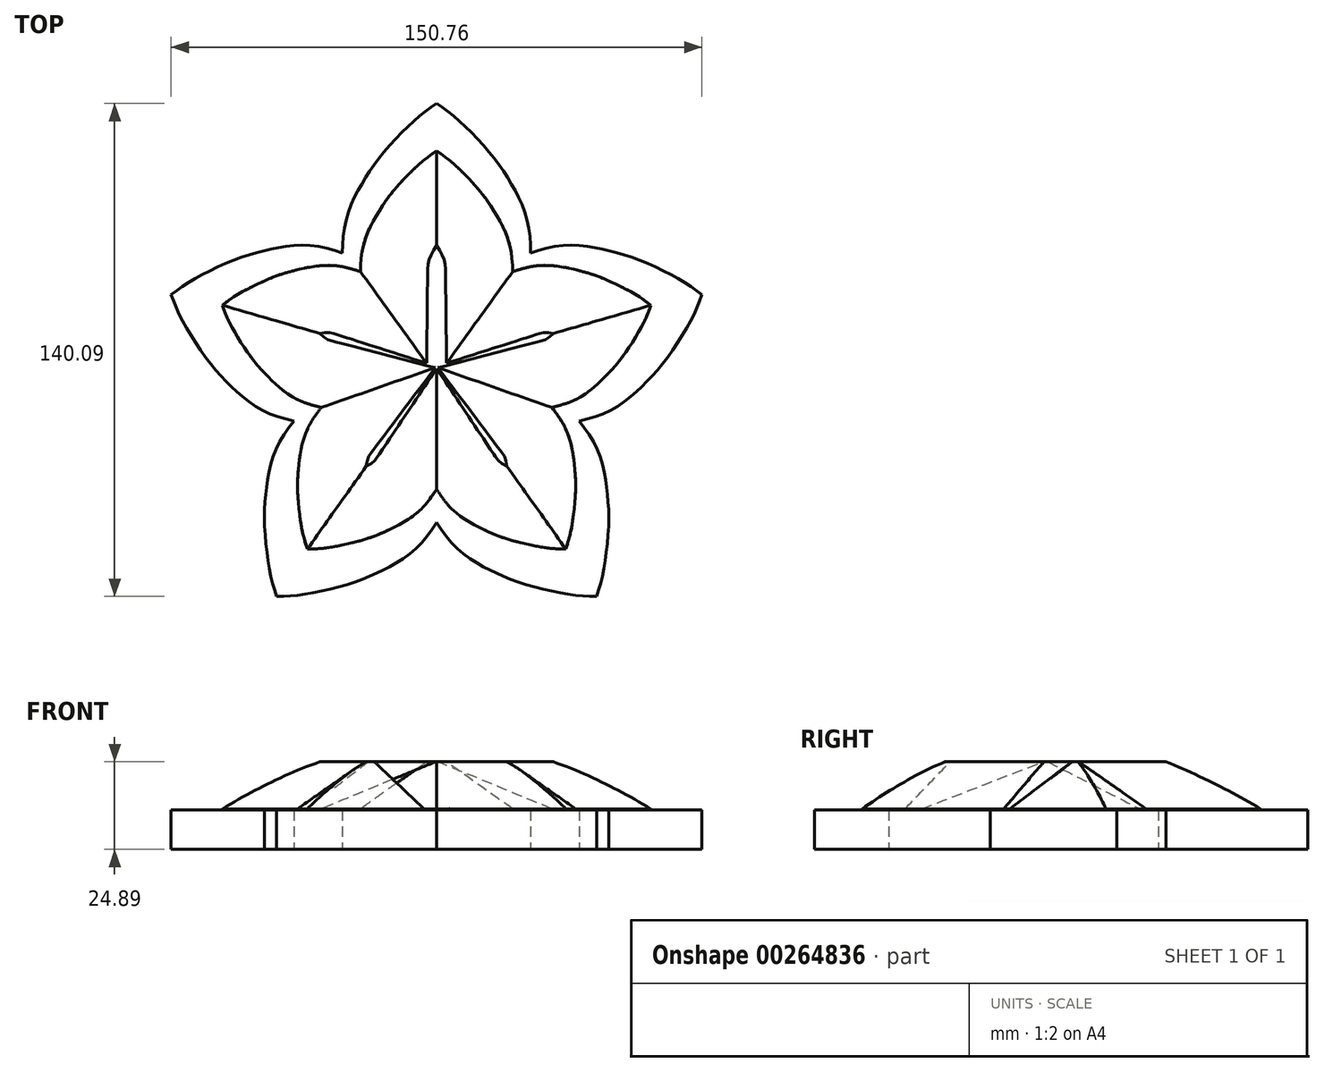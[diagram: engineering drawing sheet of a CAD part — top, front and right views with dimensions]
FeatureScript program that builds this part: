
annotation { "Feature Type Name" : "Feature", "Feature Type Description" : "" }
export const myFeature = defineFeature(function(context is Context, id is Id, definition is map)
    precondition{}
    {
        {
            var Q0;
            Q0=qCreatedBy(makeId("Top.planeOp"),FACE);
            var sketch = newSketch(context, id + "F0", { "sketchPlane" : qUnion([Q0])});
            skFitSpline(sketch, "E0.MirrorCS", {"points": [v(19.73, 114.61) * mm, v(16.52, 127.07) * mm, v(9.03, 139.64) * mm, v(3.16, 145.12) * mm, v(0, 146.87) * mm], "startDerivative": vector(-4.34, 40.29) * mm, "endDerivative": vector(-28.01, 11.55) * mm, "construction": true});
            skLineSegment(sketch, "E1", {"start": v(0, 0) * mm, "end": v(0, 146.87) * mm, "construction": true});
            skFitSpline(sketch, "E2.MirrorCS", {"points": [v(-19.73, 114.61) * mm, v(-16.52, 127.07) * mm, v(-9.03, 139.64) * mm, v(-3.16, 145.12) * mm, v(0, 146.87) * mm], "startDerivative": vector(4.34, 40.29) * mm, "endDerivative": vector(28.01, 11.55) * mm, "construction": true});
            skLineSegment(sketch, "E3", {"start": v(0, 0) * mm, "end": v(0, 0) * mm});
            skFitSpline(sketch, "E4.MirrorCS", {"points": [v(-19.73, 114.61) * mm, v(-32.36, 116) * mm, v(-46.75, 113.44) * mm, v(-53.96, 109.89) * mm, v(-56.85, 107.42) * mm], "startDerivative": vector(-39.26, 10.04) * mm, "endDerivative": vector(-20.62, -22.2) * mm, "construction": true});
            skFitSpline(sketch, "E5.MirrorCS", {"points": [v(-33.54, 77.65) * mm, v(-43.99, 84.88) * mm, v(-53.18, 96.25) * mm, v(-56.28, 103.66) * mm, v(-56.85, 107.42) * mm], "startDerivative": vector(-36.22, 18.17) * mm, "endDerivative": vector(-1, 30.28) * mm, "construction": true});
            skFitSpline(sketch, "E6.MirrorCS", {"points": [v(19.73, 114.61) * mm, v(32.36, 116) * mm, v(46.75, 113.44) * mm, v(53.96, 109.89) * mm, v(56.85, 107.42) * mm], "startDerivative": vector(39.26, 10.04) * mm, "endDerivative": vector(20.62, -22.2) * mm, "construction": true});
            skFitSpline(sketch, "E7.MirrorCS", {"points": [v(33.54, 77.65) * mm, v(43.99, 84.88) * mm, v(53.18, 96.25) * mm, v(56.28, 103.66) * mm, v(56.85, 107.42) * mm], "startDerivative": vector(36.22, 18.17) * mm, "endDerivative": vector(1, 30.28) * mm, "construction": true});
            skFitSpline(sketch, "E8.MirrorCS", {"points": [v(-33.54, 77.65) * mm, v(-39.27, 66.3) * mm, v(-41.91, 51.92) * mm, v(-41.1, 43.93) * mm, v(-39.8, 40.36) * mm], "startDerivative": vector(-23.15, -33.26) * mm, "endDerivative": vector(13.58, -27.09) * mm, "construction": true});
            skFitSpline(sketch, "E9.MirrorCS", {"points": [v(-3.76, 51.77) * mm, v(-14.18, 44.51) * mm, v(-28.06, 39.89) * mm, v(-36.09, 39.57) * mm, v(-39.8, 40.36) * mm], "startDerivative": vector(-29.7, -27.57) * mm, "endDerivative": vector(-28.72, 9.66) * mm, "construction": true});
            skFitSpline(sketch, "E10.MirrorCS", {"points": [v(33.54, 77.65) * mm, v(39.27, 66.3) * mm, v(41.91, 51.92) * mm, v(41.1, 43.93) * mm, v(39.8, 40.36) * mm], "startDerivative": vector(23.15, -33.26) * mm, "endDerivative": vector(-13.58, -27.09) * mm, "construction": true});
            skFitSpline(sketch, "E11.MirrorCS", {"points": [v(3.76, 51.77) * mm, v(14.18, 44.51) * mm, v(28.06, 39.89) * mm, v(36.09, 39.57) * mm, v(39.8, 40.36) * mm], "startDerivative": vector(29.7, -27.57) * mm, "endDerivative": vector(28.72, 9.66) * mm, "construction": true});
            skFitSpline(sketch, "E12", {"points": [v(-19.88, 115.85) * mm, v(-16.52, 127.07) * mm, v(-9.03, 139.64) * mm, v(-3.16, 145.12) * mm, v(0, 146.87) * mm], "startDerivative": vector(8.84, 38.02) * mm, "endDerivative": vector(19.62, 9.54) * mm, "construction": true});
            skFitSpline(sketch, "E13.MirrorCS", {"points": [v(19.88, 115.85) * mm, v(16.52, 127.07) * mm, v(9.03, 139.64) * mm, v(3.16, 145.12) * mm, v(0, 146.87) * mm], "startDerivative": vector(-8.84, 38.02) * mm, "endDerivative": vector(-19.62, 9.54) * mm, "construction": true});
            skLineSegment(sketch, "E14", {"start": v(-19.88, 115.85) * mm, "end": v(0, 87.57) * mm, "construction": true});
            skLineSegment(sketch, "E15", {"start": v(0, 87.57) * mm, "end": v(19.88, 115.85) * mm, "construction": true});
            skFitSpline(sketch, "E16.MirrorCS", {"points": [v(-19.88, 115.85) * mm, v(-31.58, 116.48) * mm, v(-45.93, 113.7) * mm, v(-53.08, 110.03) * mm, v(-55.8, 107.65) * mm], "startDerivative": vector(-38.76, 4.56) * mm, "endDerivative": vector(-15.62, -15.23) * mm, "construction": true});
            skFitSpline(sketch, "E17.MirrorCS", {"points": [v(-33.34, 78.44) * mm, v(-42.76, 85.4) * mm, v(-52.05, 96.7) * mm, v(-55.22, 104.08) * mm, v(-55.8, 107.65) * mm], "startDerivative": vector(-32.78, 21.19) * mm, "endDerivative": vector(-2.33, 21.69) * mm, "construction": true});
            skFitSpline(sketch, "E18.MirrorCS", {"points": [v(19.88, 115.85) * mm, v(31.58, 116.48) * mm, v(45.93, 113.7) * mm, v(53.08, 110.03) * mm, v(55.8, 107.65) * mm], "startDerivative": vector(38.76, 4.56) * mm, "endDerivative": vector(15.62, -15.23) * mm, "construction": true});
            skFitSpline(sketch, "E19.MirrorCS", {"points": [v(33.34, 78.44) * mm, v(42.76, 85.4) * mm, v(52.05, 96.7) * mm, v(55.22, 104.08) * mm, v(55.8, 107.65) * mm], "startDerivative": vector(32.78, 21.19) * mm, "endDerivative": vector(2.33, 21.69) * mm, "construction": true});
            skLineSegment(sketch, "E20", {"start": v(0, 87.57) * mm, "end": v(33.34, 78.44) * mm, "construction": true});
            skFitSpline(sketch, "E21.MirrorCS", {"points": [v(33.34, 78.44) * mm, v(37.9, 67.65) * mm, v(40.14, 53.2) * mm, v(39.1, 45.23) * mm, v(37.78, 41.87) * mm], "startDerivative": vector(17.41, -34.93) * mm, "endDerivative": vector(-9.04, -19.85) * mm, "construction": true});
            skFitSpline(sketch, "E22.MirrorCS", {"points": [v(2.7, 53.11) * mm, v(12.44, 46.6) * mm, v(26.21, 41.69) * mm, v(34.23, 41.2) * mm, v(37.78, 41.87) * mm], "startDerivative": vector(31.03, -23.67) * mm, "endDerivative": vector(21.2, 5.15) * mm, "construction": true});
            skFitSpline(sketch, "E23.MirrorCS", {"points": [v(-2.7, 53.11) * mm, v(-12.44, 46.6) * mm, v(-26.21, 41.69) * mm, v(-34.23, 41.2) * mm, v(-37.78, 41.87) * mm], "startDerivative": vector(-31.03, -23.67) * mm, "endDerivative": vector(-21.2, 5.15) * mm, "construction": true});
            skFitSpline(sketch, "E24.MirrorCS", {"points": [v(-33.34, 78.44) * mm, v(-37.9, 67.65) * mm, v(-40.14, 53.2) * mm, v(-39.1, 45.23) * mm, v(-37.78, 41.87) * mm], "startDerivative": vector(-17.41, -34.93) * mm, "endDerivative": vector(9.04, -19.85) * mm, "construction": true});
            skFitSpline(sketch, "E25", {"points": [v(0, 52.88) * mm, v(3.94, 47.68) * mm, v(8.9, 43.78) * mm, v(13.63, 41.33) * mm, v(18.94, 39.12) * mm, v(25.86, 37.25) * mm, v(32.02, 36.14) * mm, v(36.69, 35.9) * mm], "startDerivative": vector(24.52, -36.7) * mm, "endDerivative": vector(35.76, -0.94) * mm});
            skFitSpline(sketch, "E26.MirrorCS", {"points": [v(0, 52.88) * mm, v(-3.94, 47.68) * mm, v(-8.9, 43.78) * mm, v(-13.63, 41.33) * mm, v(-18.94, 39.12) * mm, v(-25.86, 37.25) * mm, v(-32.02, 36.14) * mm, v(-36.69, 35.9) * mm], "startDerivative": vector(-24.52, -36.7) * mm, "endDerivative": vector(-35.76, -0.94) * mm});
            skLineSegment(sketch, "E27", {"start": v(-36.69, 35.9) * mm, "end": v(0, 87.57) * mm, "construction": true});
            skFitSpline(sketch, "E28.MirrorCS", {"points": [v(-32.75, 76.13) * mm, v(-36.37, 70.7) * mm, v(-38.4, 64.72) * mm, v(-39.16, 59.46) * mm, v(-39.5, 53.71) * mm, v(-38.98, 46.57) * mm, v(-38, 40.39) * mm, v(-36.69, 35.9) * mm], "startDerivative": vector(-26.56, -35.25) * mm, "endDerivative": vector(10.9, -34.07) * mm});
            skFitSpline(sketch, "E29.MirrorCS", {"points": [v(32.75, 76.13) * mm, v(36.37, 70.7) * mm, v(38.4, 64.72) * mm, v(39.16, 59.46) * mm, v(39.5, 53.71) * mm, v(38.98, 46.57) * mm, v(38, 40.39) * mm, v(36.69, 35.9) * mm], "startDerivative": vector(26.56, -35.25) * mm, "endDerivative": vector(-10.9, -34.07) * mm});
            skLineSegment(sketch, "E30", {"start": v(-32.75, 76.13) * mm, "end": v(0, 87.57) * mm, "construction": true});
            skFitSpline(sketch, "E31.MirrorCS", {"points": [v(-32.75, 76.13) * mm, v(-38.96, 78.14) * mm, v(-44.28, 81.54) * mm, v(-48.15, 85.2) * mm, v(-51.99, 89.48) * mm, v(-56.03, 95.4) * mm, v(-59.1, 100.84) * mm, v(-60.88, 105.17) * mm], "startDerivative": vector(-42.73, 11.05) * mm, "endDerivative": vector(-12.67, 33.45) * mm});
            skFitSpline(sketch, "E32.MirrorCS", {"points": [v(-21.6, 114.72) * mm, v(-27.92, 116.34) * mm, v(-34.23, 116.3) * mm, v(-39.46, 115.28) * mm, v(-44.99, 113.7) * mm, v(-51.56, 110.85) * mm, v(-57.07, 107.89) * mm, v(-60.88, 105.17) * mm], "startDerivative": vector(-42.04, 13.45) * mm, "endDerivative": vector(-28.57, -21.53) * mm});
            skFitSpline(sketch, "E33.MirrorCS", {"points": [v(32.75, 76.13) * mm, v(38.96, 78.14) * mm, v(44.28, 81.54) * mm, v(48.15, 85.2) * mm, v(51.99, 89.48) * mm, v(56.03, 95.4) * mm, v(59.1, 100.84) * mm, v(60.88, 105.17) * mm], "startDerivative": vector(42.73, 11.05) * mm, "endDerivative": vector(12.67, 33.45) * mm});
            skLineSegment(sketch, "E34", {"start": v(-21.6, 114.72) * mm, "end": v(0, 87.57) * mm, "construction": true});
            skFitSpline(sketch, "E35.MirrorCS", {"points": [v(-21.6, 114.72) * mm, v(-21, 121.27) * mm, v(-18.96, 127.25) * mm, v(-16.35, 131.89) * mm, v(-13.11, 136.64) * mm, v(-8.34, 141.98) * mm, v(-3.8, 146.28) * mm, v(0, 149.04) * mm], "startDerivative": vector(0.47, 44.13) * mm, "endDerivative": vector(29.43, 20.33) * mm});
            skFitSpline(sketch, "E36.MirrorCS", {"points": [v(21.6, 114.72) * mm, v(27.92, 116.34) * mm, v(34.23, 116.3) * mm, v(39.46, 115.28) * mm, v(44.99, 113.7) * mm, v(51.56, 110.85) * mm, v(57.07, 107.89) * mm, v(60.88, 105.17) * mm], "startDerivative": vector(42.04, 13.45) * mm, "endDerivative": vector(28.57, -21.53) * mm});
            skFitSpline(sketch, "E37.MirrorCS", {"points": [v(21.6, 114.72) * mm, v(21, 121.27) * mm, v(18.96, 127.25) * mm, v(16.35, 131.89) * mm, v(13.11, 136.64) * mm, v(8.34, 141.98) * mm, v(3.8, 146.28) * mm, v(0, 149.04) * mm], "startDerivative": vector(-0.47, 44.13) * mm, "endDerivative": vector(-29.43, 20.33) * mm});
            skSolve(sketch);
        }
        {
            var Q0;
            Q0=makeQuery(id+"F0.imprint","IMPRINT",FACE,{"disambiguationData":[TD([[makeQuery(id+"F0.imprint","IMPRINT",EDGE,{"derivedFrom":sQuery(id+"F0.wireOp",EDGE,"E25")}),1.0]])]});
            extrude(context, id + "F1", {"entities" : qUnion([Q0]), "depth" : 24.9 * mm});
        }
        {
            var Q0;
            Q0=makeQuery(id+"F1.opExtrude","CAP_FACE",FACE,{"disambiguationData":[OSD([sQuery(id+"F0.wireOp",EDGE,"E25"),sQuery(id+"F0.wireOp",EDGE,"E26.MirrorCS"),sQuery(id+"F0.wireOp",EDGE,"E28.MirrorCS"),sQuery(id+"F0.wireOp",EDGE,"E29.MirrorCS"),sQuery(id+"F0.wireOp",EDGE,"E31.MirrorCS"),sQuery(id+"F0.wireOp",EDGE,"E32.MirrorCS"),sQuery(id+"F0.wireOp",EDGE,"E33.MirrorCS"),sQuery(id+"F0.wireOp",EDGE,"E35.MirrorCS"),sQuery(id+"F0.wireOp",EDGE,"E36.MirrorCS"),sQuery(id+"F0.wireOp",EDGE,"E37.MirrorCS")])],"isStart":false});
            chamfer(context, id + "F2", {"entities" : qUnion([Q0]), "chamferType" : ChamferType.OFFSET_ANGLE, "width" : 19.05 * mm, "oppositeDirection" : false, "angle" : 35 * degree, "tangentPropagation" : true});
        }
        {
            var Q0;
            Q0=qCreatedBy(makeId("Top.planeOp"),FACE);
            var sketch = newSketch(context, id + "F3", { "sketchPlane" : qUnion([Q0])});
            skFitSpline(sketch, "E38", {"points": [v(0, 43.45) * mm, v(4.88, 37) * mm, v(11.03, 32.19) * mm, v(16.88, 29.14) * mm, v(23.45, 26.41) * mm, v(32.02, 24.1) * mm, v(39.64, 22.72) * mm, v(45.42, 22.42) * mm], "startDerivative": vector(30.36, -45.44) * mm, "endDerivative": vector(44.28, -1.16) * mm});
            skFitSpline(sketch, "E39.MirrorCS", {"points": [v(0, 43.45) * mm, v(-4.88, 37) * mm, v(-11.03, 32.19) * mm, v(-16.88, 29.14) * mm, v(-23.45, 26.41) * mm, v(-32.02, 24.1) * mm, v(-39.64, 22.72) * mm, v(-45.42, 22.42) * mm], "startDerivative": vector(-30.36, -45.44) * mm, "endDerivative": vector(-44.28, -1.16) * mm});
            skFitSpline(sketch, "E40.MirrorCS", {"points": [v(-40.55, 72.24) * mm, v(-45.03, 65.51) * mm, v(-47.55, 58.11) * mm, v(-48.5, 51.6) * mm, v(-48.9, 44.48) * mm, v(-48.26, 35.63) * mm, v(-47.05, 27.98) * mm, v(-45.42, 22.42) * mm], "startDerivative": vector(-32.89, -43.65) * mm, "endDerivative": vector(13.5, -42.18) * mm});
            skFitSpline(sketch, "E41.MirrorCS", {"points": [v(40.55, 72.24) * mm, v(45.03, 65.51) * mm, v(47.55, 58.11) * mm, v(48.5, 51.6) * mm, v(48.9, 44.48) * mm, v(48.27, 35.63) * mm, v(47.05, 27.98) * mm, v(45.42, 22.42) * mm], "startDerivative": vector(32.89, -43.65) * mm, "endDerivative": vector(-13.5, -42.18) * mm});
            skFitSpline(sketch, "E42.MirrorCS", {"points": [v(-40.55, 72.24) * mm, v(-48.24, 74.72) * mm, v(-54.82, 78.94) * mm, v(-59.62, 83.46) * mm, v(-64.37, 88.77) * mm, v(-69.38, 96.09) * mm, v(-73.19, 102.83) * mm, v(-75.38, 108.2) * mm], "startDerivative": vector(-52.9, 13.68) * mm, "endDerivative": vector(-15.7, 41.42) * mm});
            skFitSpline(sketch, "E43.MirrorCS", {"points": [v(-26.74, 120.01) * mm, v(-34.57, 122.02) * mm, v(-42.38, 121.96) * mm, v(-48.85, 120.7) * mm, v(-55.7, 118.75) * mm, v(-63.84, 115.23) * mm, v(-70.66, 111.56) * mm, v(-75.38, 108.2) * mm], "startDerivative": vector(-52.05, 16.66) * mm, "endDerivative": vector(-35.37, -26.66) * mm});
            skFitSpline(sketch, "E44.MirrorCS", {"points": [v(40.55, 72.24) * mm, v(48.24, 74.72) * mm, v(54.82, 78.94) * mm, v(59.62, 83.46) * mm, v(64.37, 88.77) * mm, v(69.38, 96.09) * mm, v(73.19, 102.83) * mm, v(75.38, 108.2) * mm], "startDerivative": vector(52.9, 13.68) * mm, "endDerivative": vector(15.7, 41.42) * mm});
            skFitSpline(sketch, "E45.MirrorCS", {"points": [v(-26.74, 120.01) * mm, v(-26, 128.13) * mm, v(-23.48, 135.53) * mm, v(-20.25, 141.27) * mm, v(-16.23, 147.16) * mm, v(-10.33, 153.78) * mm, v(-4.7, 159.1) * mm, v(0, 162.5) * mm], "startDerivative": vector(0.58, 54.65) * mm, "endDerivative": vector(36.44, 25.18) * mm});
            skFitSpline(sketch, "E46.MirrorCS", {"points": [v(26.74, 120.01) * mm, v(34.57, 122.02) * mm, v(42.39, 121.96) * mm, v(48.85, 120.7) * mm, v(55.7, 118.75) * mm, v(63.84, 115.23) * mm, v(70.67, 111.56) * mm, v(75.38, 108.2) * mm], "startDerivative": vector(52.05, 16.66) * mm, "endDerivative": vector(35.37, -26.66) * mm});
            skFitSpline(sketch, "E47.MirrorCS", {"points": [v(26.74, 120.01) * mm, v(26, 128.13) * mm, v(23.48, 135.53) * mm, v(20.25, 141.27) * mm, v(16.23, 147.16) * mm, v(10.33, 153.78) * mm, v(4.7, 159.1) * mm, v(0, 162.5) * mm], "startDerivative": vector(-0.58, 54.65) * mm, "endDerivative": vector(-36.44, 25.18) * mm});
            skSolve(sketch);
        }
        {
            var Q0;
            Q0=makeQuery(id+"F3.imprint","IMPRINT",FACE,{"disambiguationData":[TD([[makeQuery(id+"F3.imprint","IMPRINT",EDGE,{"derivedFrom":sQuery(id+"F3.wireOp",EDGE,"7b3f644b-a014-4b3a-a81c-28b0cb1f38b5")}),1.0]])]});
            var Q1;
            Q1=makeQuery(id+"F3.imprint","IMPRINT",FACE,{"disambiguationData":[TD([[makeQuery(id+"F3.imprint","IMPRINT",EDGE,{"derivedFrom":sQuery(id+"F3.wireOp",EDGE,"E38")}),1.0]])]});
            extrude(context, id + "F4", {"entities" : qUnion([Q0, Q1]), "operationType" : NewBodyOperationType.ADD, "depth" : 11.18 * mm});
        }
    });
